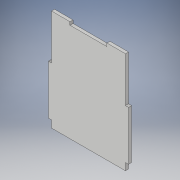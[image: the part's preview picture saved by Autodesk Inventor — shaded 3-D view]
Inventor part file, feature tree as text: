
AUTODESK INVENTOR PART (.ipt)
format: ipt  version: 2019 (Build 230136000, 136)  size: 125,440 bytes
history: native  units: in
note: dims shown in document units (in); Inventor stores cm internally (conversion verified against a paired STEP export)
features: extrude x3, sketch x3
ambient origin geometry x8: Origin, YZ Plane, XZ Plane, XY Plane, X Axis, Y Axis, Z Axis, Center Point
bodies: Solid1 (feature_tree)
feature tree (6):
  extrude  "Extrusion1"  Depth=3.111in
  extrude  "Extrusion2"  Depth=2.0in
  extrude  "Extrusion3"  Depth=0.125in
  sketch  "Sketch1"  dims[d0=3.0in d1=3.111in]
  sketch  "Sketch2"  dims[d2=0.289in d3=2.0in]
  sketch  "Sketch3"  dims[d4=0.125in d5=0.0in d6=0.125in d7=1.0in d8=0.125in d9=0.0in d10=0.125in d11=1.5in d12=0.75in d13=0.125in d14=0.0in]
